# Revit family: Haworth_Openest_FeatherSofa_AsymmetricalLeft_AP_PRELIMINARY
name_source: partatom
category: Furniture
revit_build: Autodesk Revit 2018 (Build: 20170223_1515(x64)
units: mm (PartAtom-declared; Revit-internal decimal feet)

## family parameters
Always vertical = Yes
Cut with Voids When Loaded = No
OmniClass Number = 23.40.20.00
OmniClass Title = General Furniture and Specialties
Room Calculation Point = No
Shared = No
Work Plane-Based = No

## types (3) — shared parameters
Assembly Code = E2020200
Description = Haworth - Openest - Feather - Sofa - Asymmetrical - Left
Manufacturer = Haworth
Model = SOSL
Revision No. = 1
Size = Verify Final Dim. w/ Haworth
URL = https://www.haworth.com
URL - Product = https://www.haworth.com
Warranty = http://www.haworth.com

## per-type parameters (varying)
| type | No Table |
| Without Table | Yes |
| Right Table | No |
| Left Table | No |

type visibility flags (boolean, named after types; folded from table):
- Without Table: Yes: (none)
- Right Table: Yes: Right Table
- Left Table: Yes: Left Table

## geometry (parser evidence)
native form markers: Sweep x11
no freeform markers — native parametric forms only
